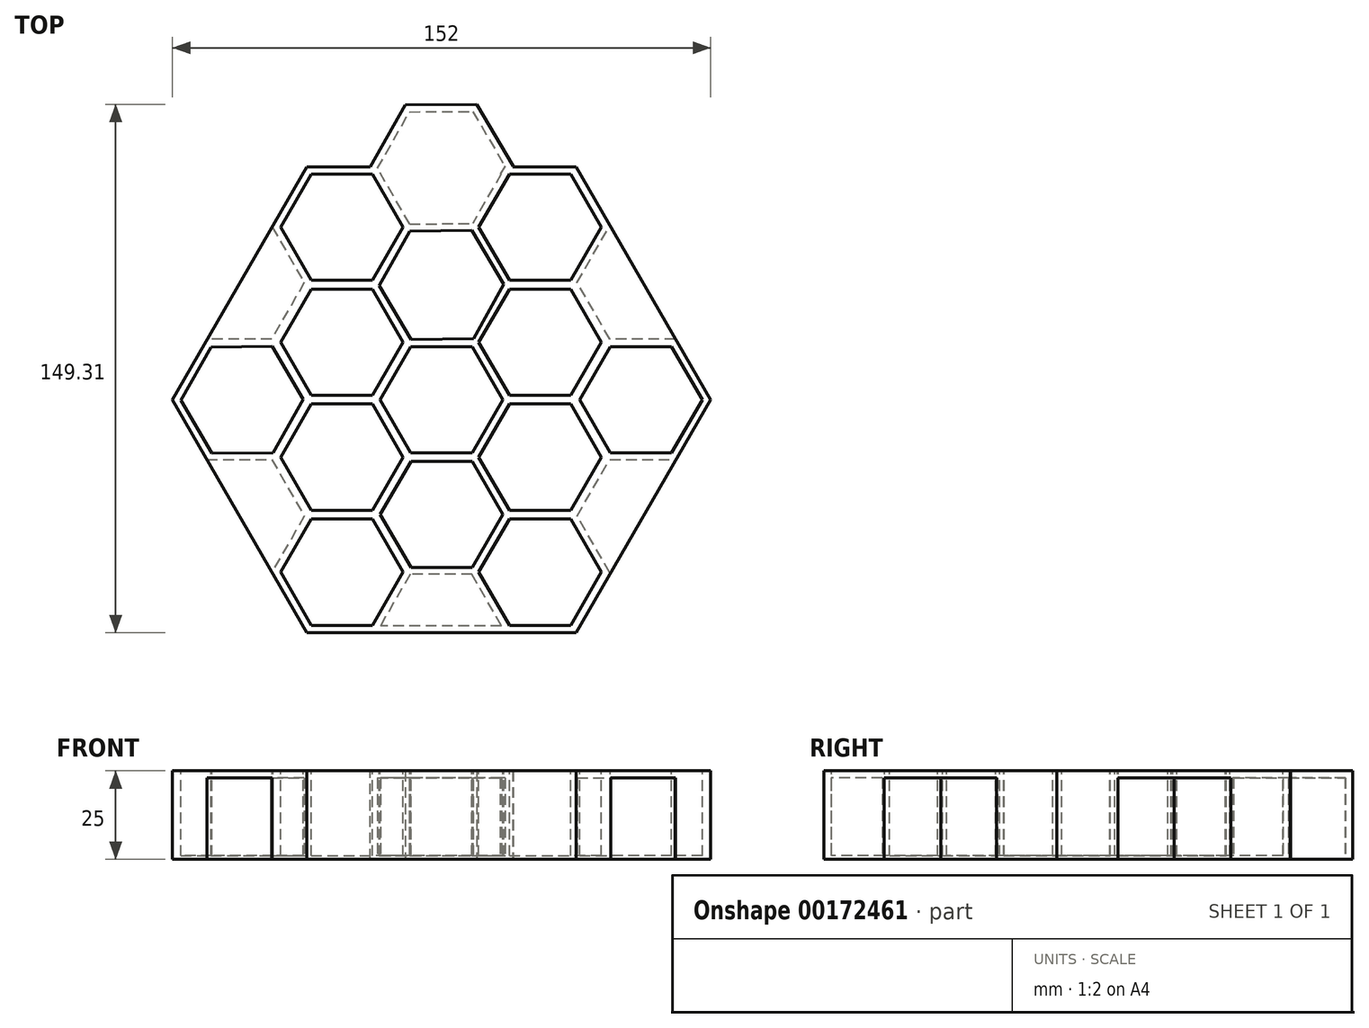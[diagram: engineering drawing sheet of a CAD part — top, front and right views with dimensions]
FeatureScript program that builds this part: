
annotation { "Feature Type Name" : "Feature", "Feature Type Description" : "" }
export const myFeature = defineFeature(function(context is Context, id is Id, definition is map)
    precondition{}
    {
        {
            var Q0;
            Q0=qCreatedBy(makeId("Top.planeOp"),FACE);
            var sketch = newSketch(context, id + "F0", { "sketchPlane" : qUnion([Q0])});
            skCircle(sketch, "E0.cCircle", {"center": v(0, 0) * mm, "radius": 76 * mm, "construction": true});
            skLineSegment(sketch, "E0.0", {"start": v(76, 0) * mm, "end": v(38, -65.82) * mm});
            skLineSegment(sketch, "E0.1", {"start": v(38, -65.82) * mm, "end": v(-38, -65.82) * mm});
            skLineSegment(sketch, "E0.2", {"start": v(-38, -65.82) * mm, "end": v(-76, 0) * mm});
            skLineSegment(sketch, "E0.3", {"start": v(-76, 0) * mm, "end": v(-38, 65.82) * mm});
            skLineSegment(sketch, "E0.4", {"start": v(-38, 65.82) * mm, "end": v(38, 65.82) * mm});
            skLineSegment(sketch, "E0.5", {"start": v(38, 65.82) * mm, "end": v(76, 0) * mm});
            skSolve(sketch);
        }
        {
            var Q0;
            Q0=makeQuery(id+"F0.imprint","IMPRINT",FACE,{"disambiguationData":[TD([[makeQuery(id+"F0.imprint","IMPRINT",EDGE,{"derivedFrom":sQuery(id+"F0.wireOp",EDGE,"E0.0")}),-1.0]])]});
            extrude(context, id + "F1", {"entities" : qUnion([Q0]), "depth" : 25 * mm});
        }
        {
            var Q0;
            Q0=makeQuery(id+"F1.opExtrude","CAP_FACE",FACE,{"disambiguationData":[OSD([sQuery(id+"F0.wireOp",EDGE,"E0.0"),sQuery(id+"F0.wireOp",EDGE,"E0.1"),sQuery(id+"F0.wireOp",EDGE,"E0.2"),sQuery(id+"F0.wireOp",EDGE,"E0.3"),sQuery(id+"F0.wireOp",EDGE,"E0.4"),sQuery(id+"F0.wireOp",EDGE,"E0.5")])],"isStart":false});
            var sketch = newSketch(context, id + "F2", { "sketchPlane" : qUnion([Q0])});
            skCircle(sketch, "E1.cCircle", {"center": v(-28.16, -48.68) * mm, "radius": 15 * mm, "construction": true});
            skLineSegment(sketch, "E1.0", {"start": v(-19.5, -63.68) * mm, "end": v(-36.82, -63.68) * mm});
            skLineSegment(sketch, "E1.1", {"start": v(-36.82, -63.68) * mm, "end": v(-45.48, -48.68) * mm});
            skLineSegment(sketch, "E1.2", {"start": v(-45.48, -48.68) * mm, "end": v(-36.82, -33.68) * mm});
            skLineSegment(sketch, "E1.3", {"start": v(-36.82, -33.68) * mm, "end": v(-19.5, -33.68) * mm});
            skLineSegment(sketch, "E1.4", {"start": v(-19.5, -33.68) * mm, "end": v(-10.84, -48.68) * mm});
            skLineSegment(sketch, "E1.5", {"start": v(-10.84, -48.68) * mm, "end": v(-19.5, -63.68) * mm});
            skCircle(sketch, "E2.0.1.0", {"center": v(-28.16, -16.18) * mm, "radius": 15 * mm, "construction": true});
            skLineSegment(sketch, "E2.0.1.1", {"start": v(-19.5, -1.18) * mm, "end": v(-10.84, -16.18) * mm});
            skLineSegment(sketch, "E2.0.1.2", {"start": v(-10.84, -16.18) * mm, "end": v(-19.5, -31.18) * mm});
            skLineSegment(sketch, "E2.0.1.3", {"start": v(-36.82, -31.18) * mm, "end": v(-45.48, -16.18) * mm});
            skLineSegment(sketch, "E2.0.1.4", {"start": v(-19.5, -31.18) * mm, "end": v(-36.82, -31.18) * mm});
            skLineSegment(sketch, "E2.0.1.5", {"start": v(-45.48, -16.18) * mm, "end": v(-36.82, -1.18) * mm});
            skLineSegment(sketch, "E2.0.1.6", {"start": v(-36.82, -1.18) * mm, "end": v(-19.5, -1.18) * mm});
            skCircle(sketch, "E2.0.2.0", {"center": v(-28.16, 16.32) * mm, "radius": 15 * mm, "construction": true});
            skLineSegment(sketch, "E2.0.2.1", {"start": v(-19.5, 31.32) * mm, "end": v(-10.84, 16.32) * mm});
            skLineSegment(sketch, "E2.0.2.2", {"start": v(-10.84, 16.32) * mm, "end": v(-19.5, 1.32) * mm});
            skLineSegment(sketch, "E2.0.2.3", {"start": v(-36.82, 1.32) * mm, "end": v(-45.48, 16.32) * mm});
            skLineSegment(sketch, "E2.0.2.4", {"start": v(-19.5, 1.32) * mm, "end": v(-36.82, 1.32) * mm});
            skLineSegment(sketch, "E2.0.2.5", {"start": v(-45.48, 16.32) * mm, "end": v(-36.82, 31.32) * mm});
            skLineSegment(sketch, "E2.0.2.6", {"start": v(-36.82, 31.32) * mm, "end": v(-19.5, 31.32) * mm});
            skCircle(sketch, "E2.0.3.0", {"center": v(-28.16, 48.82) * mm, "radius": 15 * mm, "construction": true});
            skLineSegment(sketch, "E2.0.3.1", {"start": v(-19.5, 63.82) * mm, "end": v(-10.84, 48.82) * mm});
            skLineSegment(sketch, "E2.0.3.2", {"start": v(-10.84, 48.82) * mm, "end": v(-19.5, 33.82) * mm});
            skLineSegment(sketch, "E2.0.3.3", {"start": v(-36.82, 33.82) * mm, "end": v(-45.48, 48.82) * mm});
            skLineSegment(sketch, "E2.0.3.4", {"start": v(-19.5, 33.82) * mm, "end": v(-36.82, 33.82) * mm});
            skLineSegment(sketch, "E2.0.3.5", {"start": v(-45.48, 48.82) * mm, "end": v(-36.82, 63.82) * mm});
            skLineSegment(sketch, "E2.0.3.6", {"start": v(-36.82, 63.82) * mm, "end": v(-19.5, 63.82) * mm});
            skCircle(sketch, "E2.1.0.0", {"center": v(27.84, -48.68) * mm, "radius": 15 * mm, "construction": true});
            skLineSegment(sketch, "E2.1.0.1", {"start": v(36.5, -33.68) * mm, "end": v(45.16, -48.68) * mm});
            skLineSegment(sketch, "E2.1.0.2", {"start": v(45.16, -48.68) * mm, "end": v(36.5, -63.68) * mm});
            skLineSegment(sketch, "E2.1.0.3", {"start": v(19.18, -63.68) * mm, "end": v(10.52, -48.68) * mm});
            skLineSegment(sketch, "E2.1.0.4", {"start": v(36.5, -63.68) * mm, "end": v(19.18, -63.68) * mm});
            skLineSegment(sketch, "E2.1.0.5", {"start": v(10.52, -48.68) * mm, "end": v(19.18, -33.68) * mm});
            skLineSegment(sketch, "E2.1.0.6", {"start": v(19.18, -33.68) * mm, "end": v(36.5, -33.68) * mm});
            skCircle(sketch, "E2.1.1.0", {"center": v(27.84, -16.18) * mm, "radius": 15 * mm, "construction": true});
            skLineSegment(sketch, "E2.1.1.1", {"start": v(36.5, -1.18) * mm, "end": v(45.16, -16.18) * mm});
            skLineSegment(sketch, "E2.1.1.2", {"start": v(45.16, -16.18) * mm, "end": v(36.5, -31.18) * mm});
            skLineSegment(sketch, "E2.1.1.3", {"start": v(19.18, -31.18) * mm, "end": v(10.52, -16.18) * mm});
            skLineSegment(sketch, "E2.1.1.4", {"start": v(36.5, -31.18) * mm, "end": v(19.18, -31.18) * mm});
            skLineSegment(sketch, "E2.1.1.5", {"start": v(10.52, -16.18) * mm, "end": v(19.18, -1.18) * mm});
            skLineSegment(sketch, "E2.1.1.6", {"start": v(19.18, -1.18) * mm, "end": v(36.5, -1.18) * mm});
            skCircle(sketch, "E2.1.2.0", {"center": v(27.84, 16.32) * mm, "radius": 15 * mm, "construction": true});
            skLineSegment(sketch, "E2.1.2.1", {"start": v(36.5, 31.32) * mm, "end": v(45.16, 16.32) * mm});
            skLineSegment(sketch, "E2.1.2.2", {"start": v(45.16, 16.32) * mm, "end": v(36.5, 1.32) * mm});
            skLineSegment(sketch, "E2.1.2.3", {"start": v(19.18, 1.32) * mm, "end": v(10.52, 16.32) * mm});
            skLineSegment(sketch, "E2.1.2.4", {"start": v(36.5, 1.32) * mm, "end": v(19.18, 1.32) * mm});
            skLineSegment(sketch, "E2.1.2.5", {"start": v(10.52, 16.32) * mm, "end": v(19.18, 31.32) * mm});
            skLineSegment(sketch, "E2.1.2.6", {"start": v(19.18, 31.32) * mm, "end": v(36.5, 31.32) * mm});
            skCircle(sketch, "E2.1.3.0", {"center": v(27.84, 48.82) * mm, "radius": 15 * mm, "construction": true});
            skLineSegment(sketch, "E2.1.3.1", {"start": v(36.5, 63.82) * mm, "end": v(45.16, 48.82) * mm});
            skLineSegment(sketch, "E2.1.3.2", {"start": v(45.16, 48.82) * mm, "end": v(36.5, 33.82) * mm});
            skLineSegment(sketch, "E2.1.3.3", {"start": v(19.18, 33.82) * mm, "end": v(10.52, 48.82) * mm});
            skLineSegment(sketch, "E2.1.3.4", {"start": v(36.5, 33.82) * mm, "end": v(19.18, 33.82) * mm});
            skLineSegment(sketch, "E2.1.3.5", {"start": v(10.52, 48.82) * mm, "end": v(19.18, 63.82) * mm});
            skLineSegment(sketch, "E2.1.3.6", {"start": v(19.18, 63.82) * mm, "end": v(36.5, 63.82) * mm});
            skLineSegment(sketch, "E2.direction1", {"start": v(-36.82, -63.68) * mm, "end": v(19.18, -63.68) * mm, "construction": true});
            skLineSegment(sketch, "E2.direction2", {"start": v(-36.82, -63.68) * mm, "end": v(-36.82, -31.18) * mm, "construction": true});
            skCircle(sketch, "E3.cCircle", {"center": v(0, 0) * mm, "radius": 15 * mm, "construction": true});
            skLineSegment(sketch, "E3.0", {"start": v(8.66, -15) * mm, "end": v(-8.66, -15) * mm});
            skLineSegment(sketch, "E3.1", {"start": v(-8.66, -15) * mm, "end": v(-17.32, 0) * mm});
            skLineSegment(sketch, "E3.2", {"start": v(-17.32, 0) * mm, "end": v(-8.66, 15) * mm});
            skLineSegment(sketch, "E3.3", {"start": v(-8.66, 15) * mm, "end": v(8.66, 15) * mm});
            skLineSegment(sketch, "E3.4", {"start": v(8.66, 15) * mm, "end": v(17.32, 0) * mm});
            skLineSegment(sketch, "E3.5", {"start": v(17.32, 0) * mm, "end": v(8.66, -15) * mm});
            skPoint(sketch, "E3.0.midPoint", {"position": v(0, -15) * mm});
            skCircle(sketch, "E4.cCircle", {"center": v(-56.33, 0) * mm, "radius": 15 * mm, "construction": true});
            skLineSegment(sketch, "E4.0", {"start": v(-47.8, 15.08) * mm, "end": v(-39, 0.16) * mm});
            skLineSegment(sketch, "E4.1", {"start": v(-39, 0.16) * mm, "end": v(-47.53, -14.92) * mm});
            skLineSegment(sketch, "E4.2", {"start": v(-47.53, -14.92) * mm, "end": v(-64.85, -15.08) * mm});
            skLineSegment(sketch, "E4.3", {"start": v(-64.85, -15.08) * mm, "end": v(-73.65, -0.16) * mm});
            skLineSegment(sketch, "E4.4", {"start": v(-73.65, -0.16) * mm, "end": v(-65.13, 14.92) * mm});
            skLineSegment(sketch, "E4.5", {"start": v(-65.13, 14.92) * mm, "end": v(-47.8, 15.08) * mm});
            skPoint(sketch, "E4.0.midPoint", {"position": v(-43.4, 7.62) * mm});
            skCircle(sketch, "E5.cCircle", {"center": v(56.33, 0) * mm, "radius": 15 * mm, "construction": true});
            skLineSegment(sketch, "E5.0", {"start": v(64.99, -15) * mm, "end": v(47.67, -15) * mm});
            skLineSegment(sketch, "E5.1", {"start": v(47.67, -15) * mm, "end": v(39, 0) * mm});
            skLineSegment(sketch, "E5.2", {"start": v(39, 0) * mm, "end": v(47.67, 15) * mm});
            skLineSegment(sketch, "E5.3", {"start": v(47.67, 15) * mm, "end": v(64.99, 15) * mm});
            skLineSegment(sketch, "E5.4", {"start": v(64.99, 15) * mm, "end": v(73.65, 0) * mm});
            skLineSegment(sketch, "E5.5", {"start": v(73.65, 0) * mm, "end": v(64.99, -15) * mm});
            skPoint(sketch, "E5.0.midPoint", {"position": v(56.33, -15) * mm});
            skCircle(sketch, "E6.cCircle", {"center": v(0, 32.48) * mm, "radius": 15.27 * mm, "construction": true});
            skLineSegment(sketch, "E6.0", {"start": v(8.61, 47.86) * mm, "end": v(17.63, 32.7) * mm});
            skLineSegment(sketch, "E6.1", {"start": v(17.63, 32.7) * mm, "end": v(9.01, 17.33) * mm});
            skLineSegment(sketch, "E6.2", {"start": v(9.01, 17.33) * mm, "end": v(-8.61, 17.1) * mm});
            skLineSegment(sketch, "E6.3", {"start": v(-8.61, 17.1) * mm, "end": v(-17.63, 32.25) * mm});
            skLineSegment(sketch, "E6.4", {"start": v(-17.63, 32.25) * mm, "end": v(-9.01, 47.63) * mm});
            skLineSegment(sketch, "E6.5", {"start": v(-9.01, 47.63) * mm, "end": v(8.61, 47.86) * mm});
            skPoint(sketch, "E6.0.midPoint", {"position": v(13.12, 40.28) * mm});
            skCircle(sketch, "E7.cCircle", {"center": v(0, -32.33) * mm, "radius": 14.97 * mm, "construction": true});
            skLineSegment(sketch, "E7.0", {"start": v(-8.65, -17.36) * mm, "end": v(8.65, -17.36) * mm});
            skLineSegment(sketch, "E7.1", {"start": v(8.65, -17.36) * mm, "end": v(17.3, -32.33) * mm});
            skLineSegment(sketch, "E7.2", {"start": v(17.3, -32.33) * mm, "end": v(8.65, -47.3) * mm});
            skLineSegment(sketch, "E7.3", {"start": v(8.65, -47.3) * mm, "end": v(-8.65, -47.3) * mm});
            skLineSegment(sketch, "E7.4", {"start": v(-8.65, -47.3) * mm, "end": v(-17.3, -32.33) * mm});
            skLineSegment(sketch, "E7.5", {"start": v(-17.3, -32.33) * mm, "end": v(-8.65, -17.36) * mm});
            skPoint(sketch, "E7.0.midPoint", {"position": v(0, -17.36) * mm});
            skSolve(sketch);
        }
        {
            var Q0;
            Q0=makeQuery(id+"F2.imprint","IMPRINT",FACE,{"disambiguationData":[TD([[makeQuery(id+"F2.imprint","IMPRINT",EDGE,{"derivedFrom":sQuery(id+"F2.wireOp",EDGE,"E2.1.0.1")}),-1.0]])]});
            var Q1;
            Q1=makeQuery(id+"F2.imprint","IMPRINT",FACE,{"disambiguationData":[TD([[makeQuery(id+"F2.imprint","IMPRINT",EDGE,{"derivedFrom":sQuery(id+"F2.wireOp",EDGE,"E1.0")}),-1.0]])]});
            var Q2;
            Q2=makeQuery(id+"F2.imprint","IMPRINT",FACE,{"disambiguationData":[TD([[makeQuery(id+"F2.imprint","IMPRINT",EDGE,{"derivedFrom":sQuery(id+"F2.wireOp",EDGE,"E7.0")}),-1.0]])]});
            var Q3;
            Q3=makeQuery(id+"F2.imprint","IMPRINT",FACE,{"disambiguationData":[TD([[makeQuery(id+"F2.imprint","IMPRINT",EDGE,{"derivedFrom":sQuery(id+"F2.wireOp",EDGE,"E2.0.1.1")}),-1.0]])]});
            var Q4;
            Q4=makeQuery(id+"F2.imprint","IMPRINT",FACE,{"disambiguationData":[TD([[makeQuery(id+"F2.imprint","IMPRINT",EDGE,{"derivedFrom":sQuery(id+"F2.wireOp",EDGE,"E3.0")}),-1.0]])]});
            var Q5;
            Q5=makeQuery(id+"F2.imprint","IMPRINT",FACE,{"disambiguationData":[TD([[makeQuery(id+"F2.imprint","IMPRINT",EDGE,{"derivedFrom":sQuery(id+"F2.wireOp",EDGE,"E2.1.1.1")}),-1.0]])]});
            var Q6;
            Q6=makeQuery(id+"F2.imprint","IMPRINT",FACE,{"disambiguationData":[TD([[makeQuery(id+"F2.imprint","IMPRINT",EDGE,{"derivedFrom":sQuery(id+"F2.wireOp",EDGE,"E5.0")}),-1.0]])]});
            var Q7;
            Q7=makeQuery(id+"F2.imprint","IMPRINT",FACE,{"disambiguationData":[TD([[makeQuery(id+"F2.imprint","IMPRINT",EDGE,{"derivedFrom":sQuery(id+"F2.wireOp",EDGE,"E2.1.2.1")}),-1.0]])]});
            var Q8;
            Q8=makeQuery(id+"F2.imprint","IMPRINT",FACE,{"disambiguationData":[TD([[makeQuery(id+"F2.imprint","IMPRINT",EDGE,{"derivedFrom":sQuery(id+"F2.wireOp",EDGE,"E2.1.3.1")}),-1.0]])]});
            var Q9;
            Q9=makeQuery(id+"F2.imprint","IMPRINT",FACE,{"disambiguationData":[TD([[makeQuery(id+"F2.imprint","IMPRINT",EDGE,{"derivedFrom":sQuery(id+"F2.wireOp",EDGE,"E6.0")}),-1.0]])]});
            var Q10;
            Q10=makeQuery(id+"F2.imprint","IMPRINT",FACE,{"disambiguationData":[TD([[makeQuery(id+"F2.imprint","IMPRINT",EDGE,{"derivedFrom":sQuery(id+"F2.wireOp",EDGE,"E2.0.2.1")}),-1.0]])]});
            var Q11;
            Q11=makeQuery(id+"F2.imprint","IMPRINT",FACE,{"disambiguationData":[TD([[makeQuery(id+"F2.imprint","IMPRINT",EDGE,{"derivedFrom":sQuery(id+"F2.wireOp",EDGE,"E4.0")}),-1.0]])]});
            var Q12;
            Q12=makeQuery(id+"F2.imprint","IMPRINT",FACE,{"disambiguationData":[TD([[makeQuery(id+"F2.imprint","IMPRINT",EDGE,{"derivedFrom":sQuery(id+"F2.wireOp",EDGE,"E2.0.3.1")}),-1.0]])]});
            extrude(context, id + "F3", {"entities" : qUnion([Q0, Q1, Q2, Q3, Q4, Q5, Q6, Q7, Q8, Q9, Q10, Q11, Q12]), "operationType" : NewBodyOperationType.REMOVE, "oppositeDirection" : true, "depth" : 24 * mm});
        }
        {
            var Q0;
            Q0=qCreatedBy(makeId("Top.planeOp"),FACE);
            var sketch = newSketch(context, id + "F4", { "sketchPlane" : qUnion([Q0])});
            skCircle(sketch, "E8.cCircle", {"center": v(-57.23, -32.85) * mm, "radius": 16 * mm, "construction": true});
            skLineSegment(sketch, "E8.0", {"start": v(-66.47, -16.85) * mm, "end": v(-48, -16.85) * mm});
            skLineSegment(sketch, "E8.1", {"start": v(-48, -16.85) * mm, "end": v(-38.76, -32.85) * mm});
            skLineSegment(sketch, "E8.2", {"start": v(-38.76, -32.85) * mm, "end": v(-48, -48.85) * mm});
            skLineSegment(sketch, "E8.3", {"start": v(-48, -48.85) * mm, "end": v(-66.47, -48.85) * mm});
            skLineSegment(sketch, "E8.4", {"start": v(-66.47, -48.85) * mm, "end": v(-75.7, -32.85) * mm});
            skLineSegment(sketch, "E8.5", {"start": v(-75.7, -32.85) * mm, "end": v(-66.47, -16.85) * mm});
            skPoint(sketch, "E8.0.midPoint", {"position": v(-57.23, -16.85) * mm});
            skLineSegment(sketch, "E9.0.1.0", {"start": v(-38.76, 33.15) * mm, "end": v(-48, 17.15) * mm});
            skLineSegment(sketch, "E9.0.1.1", {"start": v(-66.47, 17.15) * mm, "end": v(-75.7, 33.15) * mm});
            skLineSegment(sketch, "E9.0.1.2", {"start": v(-48, 49.15) * mm, "end": v(-38.76, 33.15) * mm});
            skLineSegment(sketch, "E9.0.1.3", {"start": v(-48, 17.15) * mm, "end": v(-66.47, 17.15) * mm});
            skLineSegment(sketch, "E9.0.1.4", {"start": v(-66.47, 49.15) * mm, "end": v(-48, 49.15) * mm});
            skLineSegment(sketch, "E9.0.1.5", {"start": v(-75.7, 33.15) * mm, "end": v(-66.47, 49.15) * mm});
            skPoint(sketch, "E9.0.1.6", {"position": v(-57.23, 49.15) * mm});
            skCircle(sketch, "E9.0.1.7", {"center": v(-57.23, 33.15) * mm, "radius": 16 * mm, "construction": true});
            skLineSegment(sketch, "E9.1.0.0", {"start": v(75.24, -32.85) * mm, "end": v(66, -48.85) * mm});
            skLineSegment(sketch, "E9.1.0.1", {"start": v(47.53, -48.85) * mm, "end": v(38.3, -32.85) * mm});
            skLineSegment(sketch, "E9.1.0.2", {"start": v(66, -16.85) * mm, "end": v(75.24, -32.85) * mm});
            skLineSegment(sketch, "E9.1.0.3", {"start": v(66, -48.85) * mm, "end": v(47.53, -48.85) * mm});
            skLineSegment(sketch, "E9.1.0.4", {"start": v(47.53, -16.85) * mm, "end": v(66, -16.85) * mm});
            skLineSegment(sketch, "E9.1.0.5", {"start": v(38.3, -32.85) * mm, "end": v(47.53, -16.85) * mm});
            skPoint(sketch, "E9.1.0.6", {"position": v(56.77, -16.85) * mm});
            skCircle(sketch, "E9.1.0.7", {"center": v(56.77, -32.85) * mm, "radius": 16 * mm, "construction": true});
            skLineSegment(sketch, "E9.1.1.0", {"start": v(75.24, 33.15) * mm, "end": v(66, 17.15) * mm});
            skLineSegment(sketch, "E9.1.1.1", {"start": v(47.53, 17.15) * mm, "end": v(38.3, 33.15) * mm});
            skLineSegment(sketch, "E9.1.1.2", {"start": v(66, 49.15) * mm, "end": v(75.24, 33.15) * mm});
            skLineSegment(sketch, "E9.1.1.3", {"start": v(66, 17.15) * mm, "end": v(47.53, 17.15) * mm});
            skLineSegment(sketch, "E9.1.1.4", {"start": v(47.53, 49.15) * mm, "end": v(66, 49.15) * mm});
            skLineSegment(sketch, "E9.1.1.5", {"start": v(38.3, 33.15) * mm, "end": v(47.53, 49.15) * mm});
            skPoint(sketch, "E9.1.1.6", {"position": v(56.77, 49.15) * mm});
            skCircle(sketch, "E9.1.1.7", {"center": v(56.77, 33.15) * mm, "radius": 16 * mm, "construction": true});
            skLineSegment(sketch, "E9.direction1", {"start": v(-66.47, -48.85) * mm, "end": v(47.53, -48.85) * mm, "construction": true});
            skLineSegment(sketch, "E9.direction2", {"start": v(-66.47, -48.85) * mm, "end": v(-66.47, 17.15) * mm, "construction": true});
            skLineSegment(sketch, "E10", {"start": v(0, 0) * mm, "end": v(0, 65.93) * mm});
            skCircle(sketch, "E11.cCircle", {"center": v(0, 65.93) * mm, "radius": 17.5 * mm, "construction": true});
            skLineSegment(sketch, "E11.0", {"start": v(20.2, 66.06) * mm, "end": v(10.22, 48.5) * mm});
            skLineSegment(sketch, "E11.1", {"start": v(10.22, 48.5) * mm, "end": v(-9.98, 48.37) * mm});
            skLineSegment(sketch, "E11.2", {"start": v(-9.98, 48.37) * mm, "end": v(-20.2, 65.8) * mm});
            skLineSegment(sketch, "E11.3", {"start": v(-20.2, 65.8) * mm, "end": v(-10.22, 83.35) * mm});
            skLineSegment(sketch, "E11.4", {"start": v(-10.22, 83.35) * mm, "end": v(9.98, 83.49) * mm});
            skLineSegment(sketch, "E11.5", {"start": v(9.98, 83.49) * mm, "end": v(20.2, 66.06) * mm});
            skPoint(sketch, "E11.0.midPoint", {"position": v(15.2, 57.28) * mm});
            skSolve(sketch);
        }
        {
            var Q0;
            {var subQ1=sQuery(id+"F4.wireOp",EDGE,"E11.0");Q0=makeQuery(id+"F4.imprint","IMPRINT",FACE,{"disambiguationData":[TD([[makeQuery(id+"F4.imprint","IMPRINT",EDGE,{"derivedFrom":subQ1}),-1.0]])]});}
            extrude(context, id + "F5", {"entities" : qUnion([Q0]), "operationType" : NewBodyOperationType.ADD, "depth" : 25 * mm});
        }
        {
            var Q0;
            Q0=makeQuery(id+"F4.imprint","IMPRINT",FACE,{"disambiguationData":[TD([[makeQuery(id+"F4.imprint","IMPRINT",EDGE,{"derivedFrom":sQuery(id+"F4.wireOp",EDGE,"E9.1.1.0")}),-1.0]])]});
            var Q1;
            Q1=makeQuery(id+"F4.imprint","IMPRINT",FACE,{"disambiguationData":[TD([[makeQuery(id+"F4.imprint","IMPRINT",EDGE,{"derivedFrom":sQuery(id+"F4.wireOp",EDGE,"E9.1.0.0")}),-1.0]])]});
            var Q2;
            Q2=makeQuery(id+"F4.imprint","IMPRINT",FACE,{"disambiguationData":[TD([[makeQuery(id+"F4.imprint","IMPRINT",EDGE,{"derivedFrom":sQuery(id+"F4.wireOp",EDGE,"E8.0")}),-1.0]])]});
            var Q3;
            Q3=makeQuery(id+"F4.imprint","IMPRINT",FACE,{"disambiguationData":[TD([[makeQuery(id+"F4.imprint","IMPRINT",EDGE,{"derivedFrom":sQuery(id+"F4.wireOp",EDGE,"E9.0.1.0")}),-1.0]])]});
            extrude(context, id + "F6", {"entities" : qUnion([Q0, Q1, Q2, Q3]), "operationType" : NewBodyOperationType.REMOVE, "depth" : 23 * mm});
        }
        {
            var Q0;
            Q0=makeQuery(id+"F5.boolean.opBoolean","MERGE",FACE,{"derivedFrom":[makeQuery(id+"F1.opExtrude","CAP_FACE",FACE,{"disambiguationData":[OSD([sQuery(id+"F0.wireOp",EDGE,"E0.0"),sQuery(id+"F0.wireOp",EDGE,"E0.1"),sQuery(id+"F0.wireOp",EDGE,"E0.2"),sQuery(id+"F0.wireOp",EDGE,"E0.3"),sQuery(id+"F0.wireOp",EDGE,"E0.4"),sQuery(id+"F0.wireOp",EDGE,"E0.5")])],"isStart":true}),makeQuery(id+"F5.opExtrude","CAP_FACE",FACE,{"disambiguationData":[OSD([sQuery(id+"F4.wireOp",EDGE,"E11.0"),sQuery(id+"F4.wireOp",EDGE,"E11.1"),sQuery(id+"F4.wireOp",EDGE,"E11.2"),sQuery(id+"F4.wireOp",EDGE,"E11.3"),sQuery(id+"F4.wireOp",EDGE,"E11.4"),sQuery(id+"F4.wireOp",EDGE,"E11.5")])],"isStart":true})]});
            shell(context, id + "F7", {"entities" : qUnion([Q0]), "thickness" : 2 * mm});
        }
    });
